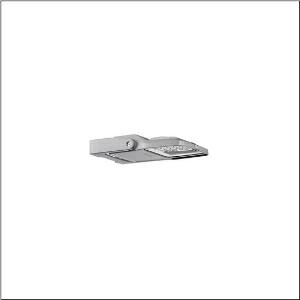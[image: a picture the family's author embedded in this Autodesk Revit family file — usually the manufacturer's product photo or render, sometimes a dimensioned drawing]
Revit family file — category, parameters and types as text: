
# Revit family: floodlight_fl_21_iq_micro___pl43_5xa7762a2a2a_df73
name_source: partatom
category: Lighting Fixtures
units: mm (PartAtom-declared; Revit-internal decimal feet)

## family parameters
Cut with Voids When Loaded = No
Host = Face
Light Source = No
Part Type = Normal
Room Calculation Point = No
Round Connector Dimension = Use Diameter
Shared = No

## types (1)
- --- (1 x LED, 3040 lm, 23.1 W, 3000K)
    Apparent Load = 23 VA
    CIE Flux Codes = 29 80 99 100 100
    Color Rendering = 70
    Color Temperature = 3000K
    Default Elevation = 1800 mm
    Description = Floodlight FL 21 iQ micro, floodlight, primary light control with lens, of PMMA, primary optical cover: protective disc, of toughened safety glass, transparent, light distribution: PL43, light emission: direct distribution, installation type: surface-mounted, LED, High Power LED, rated luminous flux: 3.040lm, luminous efficacy: 132lm/W, light colour: 730, colour temperature: 3000K, control: Auto-Match, Temp-Guard, Night-Set, Smart-Wire, Desk-Remote (wireless, voltage-free reading and setting of iQ features in the workshop via application-optimized NFC function/RFID function), optimised constant luminous flux control (CLO 2.0), Street-Remote, with terminal, 6-pole, mains connection: 220..240V, AC, 50/60Hz, start of lifetime: 23W, end of service life: 24W, reduction: 11W, luminaire housing, of diecast aluminium, powder-coated, Siteco® metallic grey (DB 702S), corrosivity category C5 mid according to DIN EN ISO 12944, sealing non-destructively replaceable, design bracket, of diecast aluminium, powder-coated, Siteco® metallic grey (DB 702S), protection rating (complete): IP66, insulation class (complete): insulation class II (safety insulation), certification: CE, ENEC, VDE, protection symbol: D, impact resistance: IK07, permissible operating ambient temperature: -40..+40°C, permissible operating ambient temperature for outdoor applications: -40..+50°C, standard: DIN EN 12944, LABS conformity tested according to VDMA 24364:2018-05, packaging unit: 1 piece

Light Distribution: PL43
    Height = 65 mm
    Lamp = 1 x LED
    Lamp Light Flux = 3040 lm
    Lamp Power = 23.1 W
    Lamp count = 1
    Length = 312 mm
    Luminous efficacy = 132 lm/W
    Manufacturer = Siteco
    ModVariant = No
    Model = 5XA7762A2A2A
    Mounting Place = Wall
    Mounting Type = Surface mounted
    Number of Poles = 1
    OnlyDefault = Yes
    Power Factor = 1
    Product Name = Floodlight FL 21 iQ micro | PL43
    Product group = floodlight | wall mounted
    ProductGroupID = 2001
    Protection Class = Protection class II
    Protection Degree = IP 66
    RLX_Detail_Level = 1
    RLX_Emergency_Light_Flux = 0 lm
    RLX_Emergency_Type = 0
    RLX_Emergency_Type_DB = No
    RlxData = <blob elided: 97337 chars, md5=4a06bb95>
    Socket = socket
    Standby Power = 0 W
    System Light Flux = 3040 lm
    System Power = 23 W
    Type Comments = factory setting: luminous flux: 100 % | dim-lin: 254 | 455 mA
    Type Image = l_1006878.jpg
    URL = http://relux.com
    VarID = @adj_109985
    Voltage = 0 V
    Weight = 0.00 kg
    Width = 230 mm

## geometry (parser evidence)
native form markers: Blend x4, Sweep x12
no freeform markers — native parametric forms only
